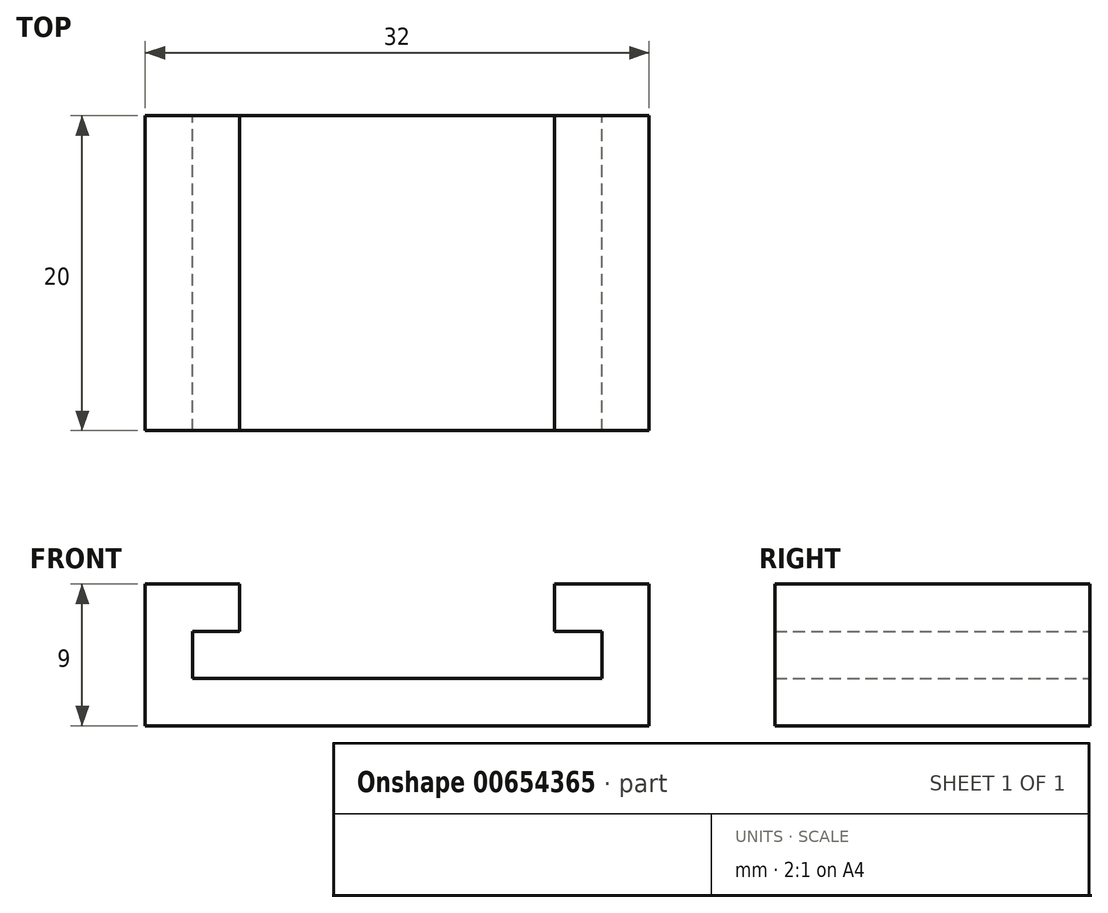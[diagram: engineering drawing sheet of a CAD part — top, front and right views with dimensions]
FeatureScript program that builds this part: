
annotation { "Feature Type Name" : "Feature", "Feature Type Description" : "" }
export const myFeature = defineFeature(function(context is Context, id is Id, definition is map)
    precondition{}
    {
        {
            var Q0;
            Q0=qCreatedBy(makeId("Front.planeOp"),FACE);
            var sketch = newSketch(context, id + "F0", { "sketchPlane" : qUnion([Q0])});
            skLineSegment(sketch, "E0.bottom", {"start": v(0, 0) * mm, "end": v(-32, 0) * mm});
            skLineSegment(sketch, "E0.top", {"start": v(-3, 3) * mm, "end": v(-29, 3) * mm});
            skLineSegment(sketch, "E0.left", {"start": v(0, 0) * mm, "end": v(0, 3) * mm});
            skLineSegment(sketch, "E0.right", {"start": v(-32, 0) * mm, "end": v(-32, 3) * mm});
            skLineSegment(sketch, "E1.top", {"start": v(-32, 9) * mm, "end": v(-29, 9) * mm});
            skLineSegment(sketch, "E1.left", {"start": v(-32, 3) * mm, "end": v(-32, 9) * mm});
            skLineSegment(sketch, "E1.right", {"start": v(-29, 3) * mm, "end": v(-29, 6) * mm});
            skLineSegment(sketch, "E2.bottom", {"start": v(-29, 9) * mm, "end": v(-26, 9) * mm});
            skLineSegment(sketch, "E2.top", {"start": v(-29, 6) * mm, "end": v(-26, 6) * mm});
            skLineSegment(sketch, "E2.right", {"start": v(-26, 9) * mm, "end": v(-26, 6) * mm});
            skLineSegment(sketch, "E3", {"start": v(-16, 0) * mm, "end": v(-16, 30) * mm, "construction": true});
            skLineSegment(sketch, "E4.MirrorCS", {"start": v(-6, 9) * mm, "end": v(-6, 6) * mm});
            skLineSegment(sketch, "E5.MirrorCS", {"start": v(-3, 6) * mm, "end": v(-6, 6) * mm});
            skLineSegment(sketch, "E6.MirrorCS", {"start": v(-3, 9) * mm, "end": v(-6, 9) * mm});
            skLineSegment(sketch, "E7.MirrorCS", {"start": v(-3, 3) * mm, "end": v(-3, 6) * mm});
            skLineSegment(sketch, "E8.MirrorCS", {"start": v(0, 3) * mm, "end": v(0, 9) * mm});
            skLineSegment(sketch, "E9.MirrorCS", {"start": v(0, 9) * mm, "end": v(-3, 9) * mm});
            skSolve(sketch);
        }
        {
            var Q0;
            Q0=makeQuery(id+"F0.imprint","IMPRINT",FACE,{"disambiguationData":[TD([[makeQuery(id+"F0.imprint","IMPRINT",EDGE,{"derivedFrom":sQuery(id+"F0.wireOp",EDGE,"E0.bottom")}),-1.0]])]});
            extrude(context, id + "F1", {"entities" : qUnion([Q0]), "depth" : 20 * mm, "offsetDistance" : 25 * mm});
        }
    });
